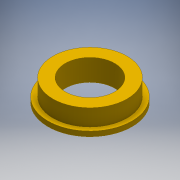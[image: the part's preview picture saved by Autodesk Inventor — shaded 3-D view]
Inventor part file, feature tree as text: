
AUTODESK INVENTOR PART (.ipt)
format: ipt  version: 2016 (Build 200138000, 138)  size: 107,008 bytes
history: native  units: mm
features: extrude x2, other x1, sketch x1
ambient origin geometry x8: Origin, YZ Plane, XZ Plane, XY Plane, X Axis, Y Axis, Z Axis, Center Point
bodies: Body1 (feature_tree)
feature tree (4):
  other  "ソリッド1"
  sketch  "スケッチ1"
  extrude  "押し出し1"  Depth=12.0mm
  extrude  "押し出し2"  Depth=8.0mm
